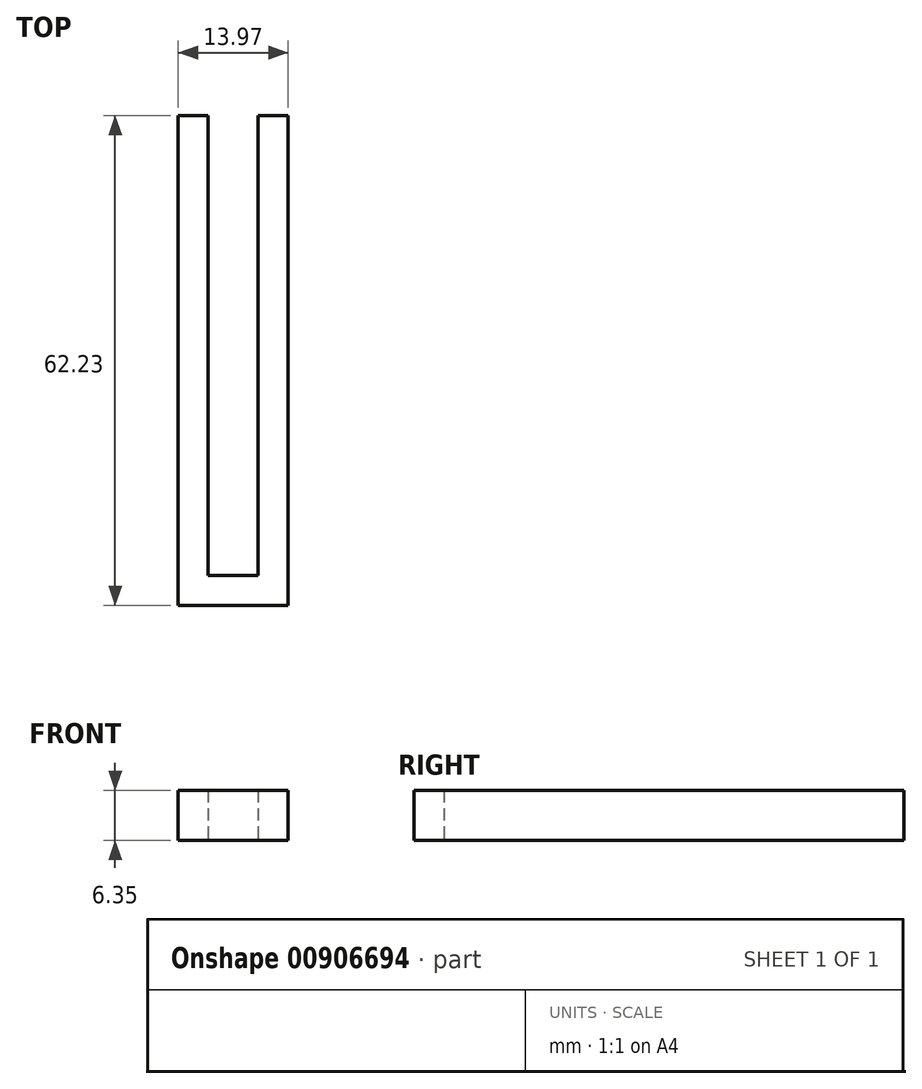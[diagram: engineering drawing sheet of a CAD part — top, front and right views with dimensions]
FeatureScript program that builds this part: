
annotation { "Feature Type Name" : "Feature", "Feature Type Description" : "" }
export const myFeature = defineFeature(function(context is Context, id is Id, definition is map)
    precondition{}
    {
        {
            var Q0;
            Q0=qCreatedBy(makeId("Top.planeOp"),FACE);
            var sketch = newSketch(context, id + "F0", { "sketchPlane" : qUnion([Q0])});
            skLineSegment(sketch, "E0.bottom", {"start": v(6.35, 0) * mm, "end": v(0, 0) * mm});
            skLineSegment(sketch, "E0.top", {"start": v(6.35, 58.42) * mm, "end": v(0, 58.42) * mm});
            skLineSegment(sketch, "E0.left", {"start": v(0, 0) * mm, "end": v(0, 58.42) * mm});
            skLineSegment(sketch, "E0.right", {"start": v(6.35, 0) * mm, "end": v(6.35, 58.42) * mm});
            skSolve(sketch);
        }
        {
            var Q0;
            Q0 = qSketchRegion(id + "F0", true);
            extrude(context, id + "F1", {"entities" : qUnion([Q0]), "depth" : 2.54 * mm, "offsetDistance" : 25.4 * mm});
        }
        {
            var Q0;
            Q0=makeQuery(id+"F1.opExtrude","CAP_FACE",FACE,{"disambiguationData":[OSD([sQuery(id+"F0.wireOp",EDGE,"E0.bottom"),sQuery(id+"F0.wireOp",EDGE,"E0.top"),sQuery(id+"F0.wireOp",EDGE,"E0.left"),sQuery(id+"F0.wireOp",EDGE,"E0.right")])],"isStart":false});
            shell(context, id + "F2", {"entities" : qUnion([Q0]), "thickness" : 3.8 * mm, "oppositeDirection" : true});
        }
        {
            var Q0;
            Q0=makeQuery(id+"F2.opShell","OFFSET_FACE",FACE,{"disambiguationData":[OSD([sQuery(id+"F0.wireOp",EDGE,"E0.bottom"),sQuery(id+"F0.wireOp",EDGE,"E0.top"),sQuery(id+"F0.wireOp",EDGE,"E0.left"),sQuery(id+"F0.wireOp",EDGE,"E0.right")])]});
            extrude(context, id + "F3", {"entities" : qUnion([Q0]), "operationType" : NewBodyOperationType.REMOVE, "oppositeDirection" : true, "depth" : 6.1 * mm, "offsetDistance" : 25.4 * mm});
        }
        {
            var Q0;
            Q0=makeQuery(id+"F1.opExtrude","SWEPT_FACE",FACE,{"disambiguationData":[OSD([sQuery(id+"F0.wireOp",EDGE,"E0.top")])]});
            var sketch = newSketch(context, id + "F4", { "sketchPlane" : qUnion([Q0])});
            skLineSegment(sketch, "E1.bottom", {"start": v(3.81, -3.8) * mm, "end": v(-10.16, -3.81) * mm});
            skLineSegment(sketch, "E1.top", {"start": v(3.81, 2.54) * mm, "end": v(-10.16, 2.54) * mm});
            skLineSegment(sketch, "E1.left", {"start": v(-10.16, -3.81) * mm, "end": v(-10.16, 2.54) * mm});
            skLineSegment(sketch, "E1.right", {"start": v(3.81, -3.8) * mm, "end": v(3.81, 2.54) * mm});
            skSolve(sketch);
        }
        {
            var Q0;
            Q0 = qSketchRegion(id + "F4", true);
            extrude(context, id + "F5", {"entities" : qUnion([Q0]), "operationType" : NewBodyOperationType.REMOVE, "oppositeDirection" : true, "depth" : 3.8 * mm, "offsetDistance" : 25.4 * mm});
        }
    });
